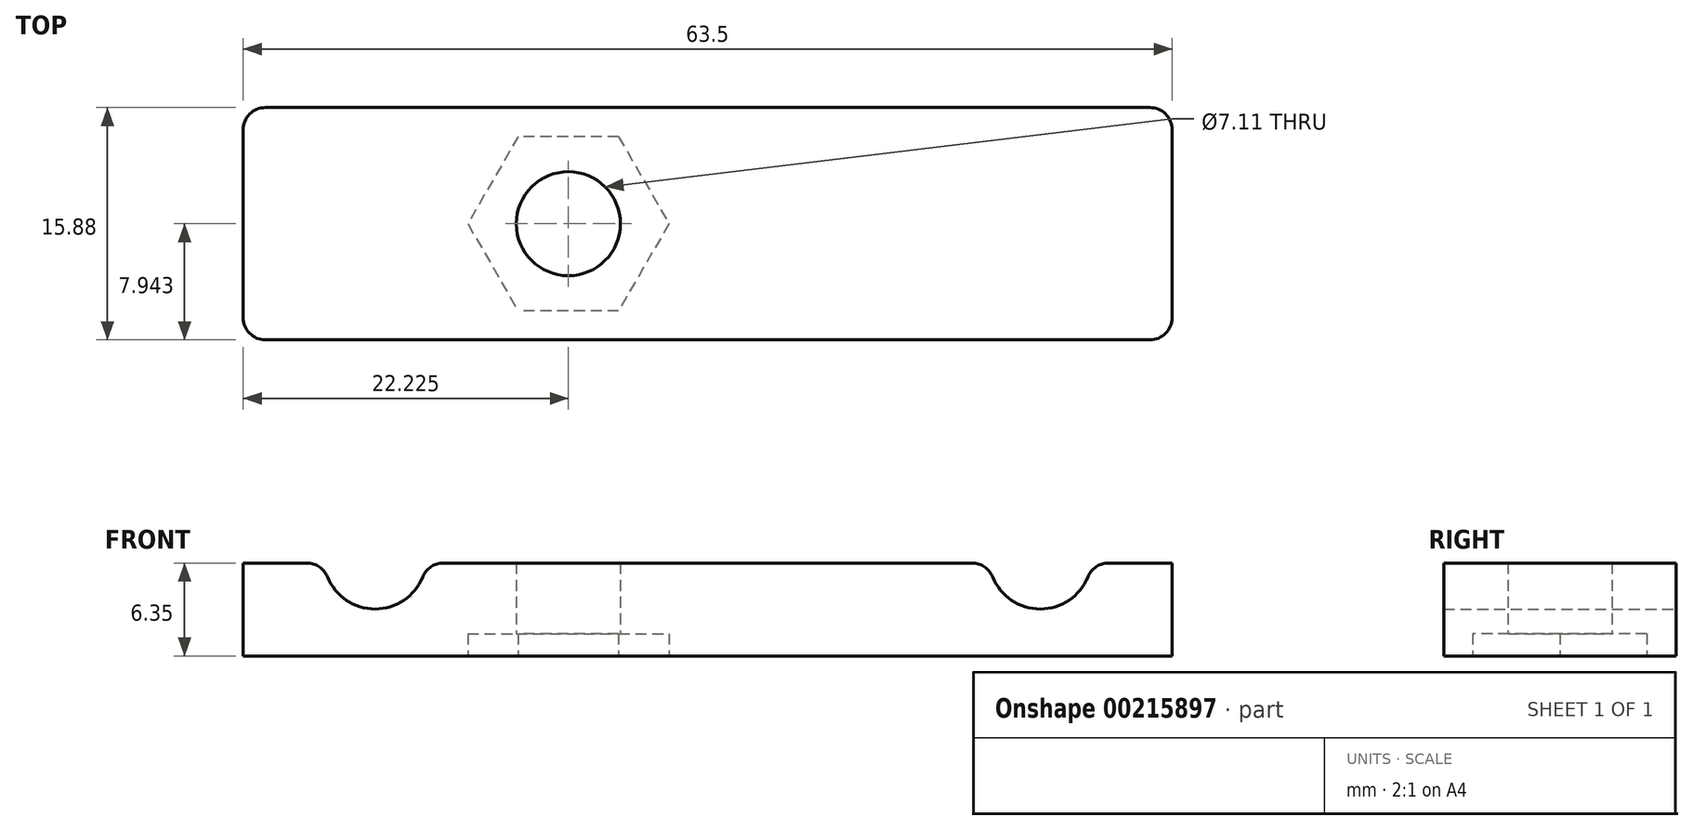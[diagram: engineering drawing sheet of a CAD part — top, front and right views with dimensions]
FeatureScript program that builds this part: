
annotation { "Feature Type Name" : "Feature", "Feature Type Description" : "" }
export const myFeature = defineFeature(function(context is Context, id is Id, definition is map)
    precondition{}
    {
        {
            var Q0;
            Q0=qCreatedBy(makeId("Top.planeOp"),FACE);
            var sketch = newSketch(context, id + "F0", { "sketchPlane" : qUnion([Q0])});
            skLineSegment(sketch, "E0", {"start": v(-31.75, 0) * mm, "end": v(-31.75, -15.88) * mm});
            skLineSegment(sketch, "E1", {"start": v(-31.75, -15.88) * mm, "end": v(0, -15.88) * mm});
            skLineSegment(sketch, "E2", {"start": v(-31.75, 0) * mm, "end": v(0, 0) * mm});
            skLineSegment(sketch, "E3.MirrorCS", {"start": v(31.75, 0) * mm, "end": v(0, 0) * mm});
            skLineSegment(sketch, "E4.MirrorCS", {"start": v(31.75, -15.88) * mm, "end": v(0, -15.88) * mm});
            skLineSegment(sketch, "E5.MirrorCS", {"start": v(31.75, 0) * mm, "end": v(31.75, -15.88) * mm});
            skSolve(sketch);
        }
        {
            var Q0;
            Q0=qSketchRegion(id+"F0",true);
            extrude(context, id + "F1", {"entities" : qUnion([Q0]), "depth" : 6.35 * mm});
        }
        {
            var Q0;
            Q0=makeQuery(id+"F1.opExtrude","SWEPT_FACE",FACE,{"disambiguationData":[OSD([sQuery(id+"F0.wireOp",EDGE,"E2"),sQuery(id+"F0.wireOp",EDGE,"E3.MirrorCS")])]});
            var sketch = newSketch(context, id + "F2", { "sketchPlane" : qUnion([Q0])});
            skCircle(sketch, "E6", {"center": v(-22.73, 6.73) * mm, "radius": 3.52 * mm});
            skCircle(sketch, "E7", {"center": v(22.73, 6.73) * mm, "radius": 3.52 * mm});
            skSolve(sketch);
        }
        {
            var Q0;
            Q0 = qSketchRegion(id + "F2", true);
            extrude(context, id + "F3", {"entities" : qUnion([Q0]), "operationType" : NewBodyOperationType.REMOVE, "endBound" : BoundingType.THROUGH_ALL, "oppositeDirection" : true, "depth" : 25.4 * mm});
        }
        {
            var Q0;
            Q0=makeQuery(id+"F1.opExtrude","SWEPT_EDGE",EDGE,{"disambiguationData":[OSD([sQuery(id+"F0.wireOp",EDGE,"E3.MirrorCS"),sQuery(id+"F0.wireOp",EDGE,"E5.MirrorCS")])]});
            var Q1;
            Q1=makeQuery(id+"F1.opExtrude","SWEPT_EDGE",EDGE,{"disambiguationData":[OSD([sQuery(id+"F0.wireOp",EDGE,"E4.MirrorCS"),sQuery(id+"F0.wireOp",EDGE,"E5.MirrorCS")])]});
            var Q2;
            Q2=makeQuery(id+"F1.opExtrude","SWEPT_EDGE",EDGE,{"disambiguationData":[OSD([sQuery(id+"F0.wireOp",EDGE,"E0"),sQuery(id+"F0.wireOp",EDGE,"E2")])]});
            var Q3;
            Q3=makeQuery(id+"F1.opExtrude","SWEPT_EDGE",EDGE,{"disambiguationData":[OSD([sQuery(id+"F0.wireOp",EDGE,"E0"),sQuery(id+"F0.wireOp",EDGE,"E1")])]});
            var Q4;
            {var subQ0=sQuery(id+"F2.wireOp",EDGE,"E6");var subQ1=sQuery(id+"F0.wireOp",EDGE,"E3.MirrorCS");var subQ2=sQuery(id+"F0.wireOp",EDGE,"E2");var subQ3=makeQuery(id+"F1.opExtrude","CAP_EDGE",EDGE,{"disambiguationData":[OSD([subQ2,subQ1])],"isStart":false});var subQ4=makeQuery(id+"F2.imprint","INTERSECT",VERTEX,{"disambiguationData":[OD(0.0)],"derivedFrom":[subQ3,subQ0]});Q4=makeQuery(id+"F3.boolean.opBoolean","COPY",EDGE,{"derivedFrom":makeQuery(id+"F3.opExtrude","TWEAK_EDGE",EDGE,{"disambiguationData":[OD(1.0)],"derivedFrom":[makeQuery(id+"F1.opExtrude","CAP_FACE",FACE,{"disambiguationData":[OSD([sQuery(id+"F0.wireOp",EDGE,"E0"),sQuery(id+"F0.wireOp",EDGE,"E1"),subQ2,subQ1,sQuery(id+"F0.wireOp",EDGE,"E4.MirrorCS"),sQuery(id+"F0.wireOp",EDGE,"E5.MirrorCS")])],"isStart":false}),makeQuery(id+"F2.imprint","IMPRINT",EDGE,{"disambiguationData":[TD([[subQ4,1.0]])],"derivedFrom":subQ0}),makeQuery(id+"F2.imprint","IMPRINT",EDGE,{"disambiguationData":[TD([[subQ4,-1.0]])],"derivedFrom":subQ0})]})});}
            var Q5;
            {var subQ0=sQuery(id+"F2.wireOp",EDGE,"E6");var subQ1=sQuery(id+"F0.wireOp",EDGE,"E3.MirrorCS");var subQ2=sQuery(id+"F0.wireOp",EDGE,"E2");var subQ3=makeQuery(id+"F1.opExtrude","CAP_EDGE",EDGE,{"disambiguationData":[OSD([subQ2,subQ1])],"isStart":false});var subQ4=makeQuery(id+"F2.imprint","INTERSECT",VERTEX,{"disambiguationData":[OD(0.0)],"derivedFrom":[subQ3,subQ0]});Q5=makeQuery(id+"F3.boolean.opBoolean","COPY",EDGE,{"derivedFrom":makeQuery(id+"F3.opExtrude","TWEAK_EDGE",EDGE,{"disambiguationData":[OD(0.0)],"derivedFrom":[makeQuery(id+"F1.opExtrude","CAP_FACE",FACE,{"disambiguationData":[OSD([sQuery(id+"F0.wireOp",EDGE,"E0"),sQuery(id+"F0.wireOp",EDGE,"E1"),subQ2,subQ1,sQuery(id+"F0.wireOp",EDGE,"E4.MirrorCS"),sQuery(id+"F0.wireOp",EDGE,"E5.MirrorCS")])],"isStart":false}),makeQuery(id+"F2.imprint","IMPRINT",EDGE,{"disambiguationData":[TD([[subQ4,1.0]])],"derivedFrom":subQ0}),makeQuery(id+"F2.imprint","IMPRINT",EDGE,{"disambiguationData":[TD([[subQ4,-1.0]])],"derivedFrom":subQ0})]})});}
            var Q6;
            {var subQ0=sQuery(id+"F2.wireOp",EDGE,"E7");var subQ1=sQuery(id+"F0.wireOp",EDGE,"E3.MirrorCS");var subQ2=sQuery(id+"F0.wireOp",EDGE,"E2");var subQ3=makeQuery(id+"F1.opExtrude","CAP_EDGE",EDGE,{"disambiguationData":[OSD([subQ2,subQ1])],"isStart":false});var subQ4=makeQuery(id+"F2.imprint","INTERSECT",VERTEX,{"disambiguationData":[OD(0.0)],"derivedFrom":[subQ3,subQ0]});Q6=makeQuery(id+"F3.boolean.opBoolean","COPY",EDGE,{"derivedFrom":makeQuery(id+"F3.opExtrude","TWEAK_EDGE",EDGE,{"disambiguationData":[OD(1.0)],"derivedFrom":[makeQuery(id+"F1.opExtrude","CAP_FACE",FACE,{"disambiguationData":[OSD([sQuery(id+"F0.wireOp",EDGE,"E0"),sQuery(id+"F0.wireOp",EDGE,"E1"),subQ2,subQ1,sQuery(id+"F0.wireOp",EDGE,"E4.MirrorCS"),sQuery(id+"F0.wireOp",EDGE,"E5.MirrorCS")])],"isStart":false}),makeQuery(id+"F2.imprint","IMPRINT",EDGE,{"disambiguationData":[TD([[subQ4,-1.0]])],"derivedFrom":subQ0}),makeQuery(id+"F2.imprint","IMPRINT",EDGE,{"disambiguationData":[TD([[subQ4,1.0]])],"derivedFrom":subQ0})]})});}
            var Q7;
            {var subQ0=sQuery(id+"F2.wireOp",EDGE,"E7");var subQ1=sQuery(id+"F0.wireOp",EDGE,"E3.MirrorCS");var subQ2=sQuery(id+"F0.wireOp",EDGE,"E2");var subQ3=makeQuery(id+"F1.opExtrude","CAP_EDGE",EDGE,{"disambiguationData":[OSD([subQ2,subQ1])],"isStart":false});var subQ4=makeQuery(id+"F2.imprint","INTERSECT",VERTEX,{"disambiguationData":[OD(0.0)],"derivedFrom":[subQ3,subQ0]});Q7=makeQuery(id+"F3.boolean.opBoolean","COPY",EDGE,{"derivedFrom":makeQuery(id+"F3.opExtrude","TWEAK_EDGE",EDGE,{"disambiguationData":[OD(0.0)],"derivedFrom":[makeQuery(id+"F1.opExtrude","CAP_FACE",FACE,{"disambiguationData":[OSD([sQuery(id+"F0.wireOp",EDGE,"E0"),sQuery(id+"F0.wireOp",EDGE,"E1"),subQ2,subQ1,sQuery(id+"F0.wireOp",EDGE,"E4.MirrorCS"),sQuery(id+"F0.wireOp",EDGE,"E5.MirrorCS")])],"isStart":false}),makeQuery(id+"F2.imprint","IMPRINT",EDGE,{"disambiguationData":[TD([[subQ4,-1.0]])],"derivedFrom":subQ0}),makeQuery(id+"F2.imprint","IMPRINT",EDGE,{"disambiguationData":[TD([[subQ4,1.0]])],"derivedFrom":subQ0})]})});}
            var Q8;
            Q8=makeQuery(id+"F3.boolean.opBoolean","INTERSECT",EDGE,{"disambiguationData":[OD(0.0)],"derivedFrom":[makeQuery(id+"F1.opExtrude","CAP_FACE",FACE,{"disambiguationData":[OSD([sQuery(id+"F0.wireOp",EDGE,"E0"),sQuery(id+"F0.wireOp",EDGE,"E1"),sQuery(id+"F0.wireOp",EDGE,"E2"),sQuery(id+"F0.wireOp",EDGE,"E3.MirrorCS"),sQuery(id+"F0.wireOp",EDGE,"E4.MirrorCS"),sQuery(id+"F0.wireOp",EDGE,"E5.MirrorCS")])],"isStart":false}),makeQuery(id+"F3.opExtrude","SWEPT_FACE",FACE,{"disambiguationData":[OSD([sQuery(id+"F2.wireOp",EDGE,"E7")])]})]});
            var Q9;
            Q9=makeQuery(id+"F3.boolean.opBoolean","INTERSECT",EDGE,{"disambiguationData":[OD(1.0)],"derivedFrom":[makeQuery(id+"F1.opExtrude","CAP_FACE",FACE,{"disambiguationData":[OSD([sQuery(id+"F0.wireOp",EDGE,"E0"),sQuery(id+"F0.wireOp",EDGE,"E1"),sQuery(id+"F0.wireOp",EDGE,"E2"),sQuery(id+"F0.wireOp",EDGE,"E3.MirrorCS"),sQuery(id+"F0.wireOp",EDGE,"E4.MirrorCS"),sQuery(id+"F0.wireOp",EDGE,"E5.MirrorCS")])],"isStart":false}),makeQuery(id+"F3.opExtrude","SWEPT_FACE",FACE,{"disambiguationData":[OSD([sQuery(id+"F2.wireOp",EDGE,"E7")])]})]});
            var Q10;
            Q10=makeQuery(id+"F3.boolean.opBoolean","INTERSECT",EDGE,{"disambiguationData":[OD(1.0)],"derivedFrom":[makeQuery(id+"F1.opExtrude","CAP_FACE",FACE,{"disambiguationData":[OSD([sQuery(id+"F0.wireOp",EDGE,"E0"),sQuery(id+"F0.wireOp",EDGE,"E1"),sQuery(id+"F0.wireOp",EDGE,"E2"),sQuery(id+"F0.wireOp",EDGE,"E3.MirrorCS"),sQuery(id+"F0.wireOp",EDGE,"E4.MirrorCS"),sQuery(id+"F0.wireOp",EDGE,"E5.MirrorCS")])],"isStart":false}),makeQuery(id+"F3.opExtrude","SWEPT_FACE",FACE,{"disambiguationData":[OSD([sQuery(id+"F2.wireOp",EDGE,"E6")])]})]});
            var Q11;
            Q11=makeQuery(id+"F3.boolean.opBoolean","INTERSECT",EDGE,{"disambiguationData":[OD(0.0)],"derivedFrom":[makeQuery(id+"F1.opExtrude","CAP_FACE",FACE,{"disambiguationData":[OSD([sQuery(id+"F0.wireOp",EDGE,"E0"),sQuery(id+"F0.wireOp",EDGE,"E1"),sQuery(id+"F0.wireOp",EDGE,"E2"),sQuery(id+"F0.wireOp",EDGE,"E3.MirrorCS"),sQuery(id+"F0.wireOp",EDGE,"E4.MirrorCS"),sQuery(id+"F0.wireOp",EDGE,"E5.MirrorCS")])],"isStart":false}),makeQuery(id+"F3.opExtrude","SWEPT_FACE",FACE,{"disambiguationData":[OSD([sQuery(id+"F2.wireOp",EDGE,"E6")])]})]});
            fillet(context, id + "F4", {"entities" : qUnion([Q0, Q1, Q2, Q3, Q4, Q5, Q6, Q7, Q8, Q9, Q10, Q11]), "radius" : 1.52 * mm, "tangentPropagation" : true, "allowEdgeOverflow" : false});
        }
        {
            var Q0;
            {var subQ0=sQuery(id+"F0.wireOp",EDGE,"E5.MirrorCS");var subQ1=sQuery(id+"F0.wireOp",EDGE,"E4.MirrorCS");var subQ2=sQuery(id+"F0.wireOp",EDGE,"E3.MirrorCS");var subQ3=sQuery(id+"F0.wireOp",EDGE,"E2");var subQ4=sQuery(id+"F0.wireOp",EDGE,"E1");var subQ5=sQuery(id+"F0.wireOp",EDGE,"E0");Q0=makeQuery(id+"Fc8Fx7NPbMqCv0M_1.boolean.opBoolean","MERGE",FACE,{"derivedFrom":[makeQuery(id+"F1.opExtrude","CAP_FACE",FACE,{"disambiguationData":[OSD([subQ5,subQ4,subQ3,subQ2,subQ1,subQ0])],"isStart":true}),makeQuery(id+"Fc8Fx7NPbMqCv0M_1.opExtrude","CAP_FACE",FACE,{"disambiguationData":[OSD([subQ5,subQ4,subQ3,subQ2,subQ1,subQ0])],"isStart":false})]});}
            var sketch = newSketch(context, id + "F5", { "sketchPlane" : qUnion([Q0])});
            skCircle(sketch, "E8", {"center": v(-9.53, 7.94) * mm, "radius": 3.56 * mm});
            skSolve(sketch);
        }
        {
            var Q0;
            Q0=qSketchRegion(id+"F5",true);
            extrude(context, id + "F6", {"entities" : qUnion([Q0]), "operationType" : NewBodyOperationType.REMOVE, "endBound" : BoundingType.UP_TO_NEXT, "oppositeDirection" : true, "depth" : 25.4 * mm});
        }
        {
            var Q0;
            Q0=makeQuery(id+"F1.opExtrude","CAP_FACE",FACE,{"disambiguationData":[OSD([sQuery(id+"F0.wireOp",EDGE,"E0"),sQuery(id+"F0.wireOp",EDGE,"E1"),sQuery(id+"F0.wireOp",EDGE,"E2"),sQuery(id+"F0.wireOp",EDGE,"E3.MirrorCS"),sQuery(id+"F0.wireOp",EDGE,"E4.MirrorCS"),sQuery(id+"F0.wireOp",EDGE,"E5.MirrorCS")])],"isStart":true});
            var sketch = newSketch(context, id + "F7", { "sketchPlane" : qUnion([Q0])});
            skLineSegment(sketch, "E9", {"start": v(-9.53, 7.94) * mm, "end": v(4.05, 7.94) * mm, "construction": true});
            skLineSegment(sketch, "E10", {"start": v(-1.8, -5.43) * mm, "end": v(-9.53, 7.94) * mm, "construction": true});
            skLineSegment(sketch, "E11", {"start": v(-9.53, 7.94) * mm, "end": v(-1.58, 21.7) * mm, "construction": true});
            skLineSegment(sketch, "E12", {"start": v(-9.52, 7.94) * mm, "end": v(-9.52, -7.63) * mm, "construction": true});
            skLineSegment(sketch, "E13", {"start": v(-9.53, 7.94) * mm, "end": v(-9.53, 22.47) * mm, "construction": true});
            skLineSegment(sketch, "E14", {"start": v(-6.09, 1.98) * mm, "end": v(-2.65, 7.94) * mm});
            skLineSegment(sketch, "E15", {"start": v(-2.65, 7.94) * mm, "end": v(-6.09, 13.9) * mm});
            skLineSegment(sketch, "E16", {"start": v(-6.09, 13.9) * mm, "end": v(-9.53, 13.9) * mm});
            skLineSegment(sketch, "E17", {"start": v(-6.09, 1.98) * mm, "end": v(-9.52, 1.98) * mm});
            skLineSegment(sketch, "E18.MirrorCS", {"start": v(-12.96, 13.9) * mm, "end": v(-9.53, 13.9) * mm});
            skLineSegment(sketch, "E19.MirrorCS", {"start": v(-16.4, 7.94) * mm, "end": v(-12.96, 13.9) * mm});
            skLineSegment(sketch, "E20.MirrorCS", {"start": v(-12.96, 1.98) * mm, "end": v(-9.52, 1.98) * mm});
            skLineSegment(sketch, "E21.MirrorCS", {"start": v(-12.96, 1.98) * mm, "end": v(-16.4, 7.94) * mm});
            skSolve(sketch);
        }
        {
            var Q0;
            Q0 = qSketchRegion(id + "F7", true);
            extrude(context, id + "F8", {"entities" : qUnion([Q0]), "operationType" : NewBodyOperationType.REMOVE, "oppositeDirection" : true, "depth" : 1.52 * mm});
        }
    });
